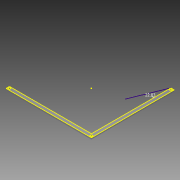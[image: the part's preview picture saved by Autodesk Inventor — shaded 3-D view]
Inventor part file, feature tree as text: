
AUTODESK INVENTOR PART (.ipt)
format: ipt  version: 2013 (Build 170138000, 138)  size: 163,328 bytes
history: native  units: in
note: dims shown in document units (in); Inventor stores cm internally (conversion verified against a paired STEP export)
features: extrude x6, sketch x5, reference x1
ambient origin geometry x8: Origin, YZ Plane, XZ Plane, XY Plane, X Axis, Y Axis, Z Axis, Center Point
bodies: Solid1 (feature_tree)
feature tree (12):
  extrude  "Extrusion1"  Depth=5.75in
  extrude  "Extrusion2"  TaperAngle=0.0deg  [1 undecoded]
  extrude  "Extrusion3"  Depth=0.25in TaperAngle=0.0deg
  extrude  "Extrusion4"  Depth=0.25in
  extrude  "Extrusion5"  Depth=0.125in
  extrude  "Extrusion6"  Depth=0.125in
  sketch  "Sketch2"  dims[d0=11.0in d2=5.75in]
  sketch  "Sketch3"  dims[d4=5.75in d6=0.0in]
  sketch  "Sketch4"  dims[d9=12.5in d10=0.25in d11=0.0in]
  sketch  "Sketch5"  dims[d12=0.25in d13=0.25in]
  reference  "Reference1"
  sketch  "Sketch6"  dims[d14=0.25in d15=0.125in d16=0.125in d20=0.5in d22=0.125in d23=0.25in d24=0.25in d25=0.25in d26=0.0in d27=0.125in d28=1.0in d29=0.0in d30=0.5in d31=11.5in d32=0.0in d33=0.5in d34=0.5in d35=0.25in d36=0.25in d37=0.125in d38=0.125in d39=0.25in d40=0.25in d41=0.125in d42=0.125in d43=1.0in d44=0.0in d47=0.875in d48=11.125in d49=0.25in d50=0.0in d51=0.266in d52=0.266in d55=0.25in d56=0.5in d57=0.25in d58=0.0in d59=0.5in d60=4.25in]
note: 1 required parameter value undecoded (feature->parameter linkage not recoverable at this tier; creation-order binding heuristic only, values carry confidence <= 0.55)
